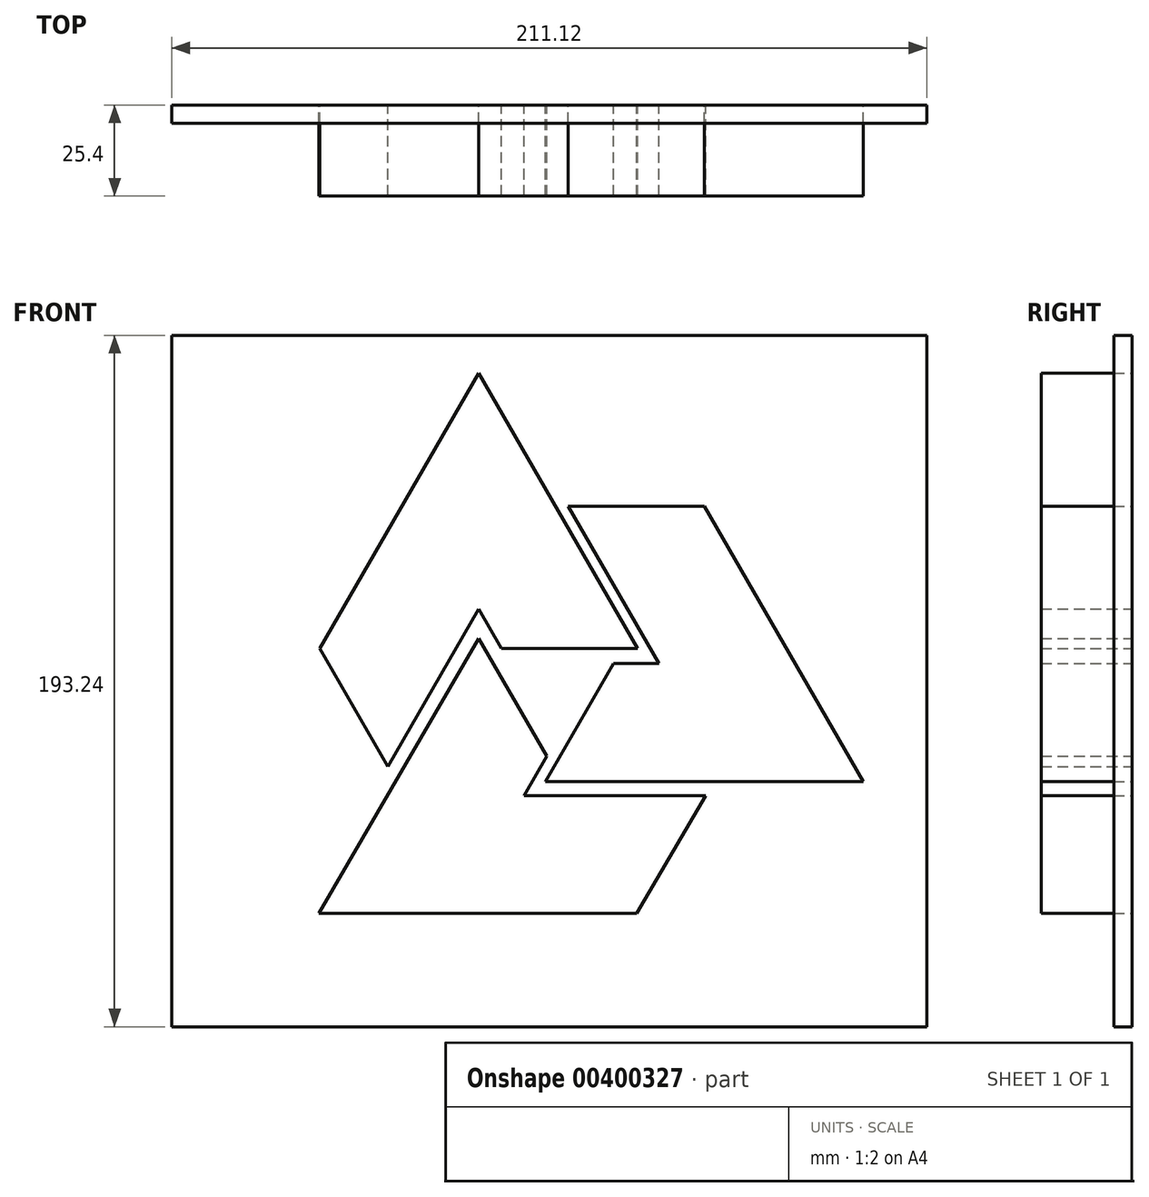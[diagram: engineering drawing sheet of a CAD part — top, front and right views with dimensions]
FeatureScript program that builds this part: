
annotation { "Feature Type Name" : "Feature", "Feature Type Description" : "" }
export const myFeature = defineFeature(function(context is Context, id is Id, definition is map)
    precondition{}
    {
        {
            var Q0;
            Q0=qCreatedBy(makeId("Front.planeOp"),FACE);
            var sketch = newSketch(context, id + "F0", { "sketchPlane" : qUnion([Q0])});
            skLineSegment(sketch, "E0", {"start": v(-33.33, -43.73) * mm, "end": v(55.57, -43.73) * mm});
            skLineSegment(sketch, "E1", {"start": v(55.57, -43.73) * mm, "end": v(74.77, -10.9) * mm});
            skLineSegment(sketch, "E2", {"start": v(-33.33, -43.73) * mm, "end": v(11.33, 33.14) * mm});
            skLineSegment(sketch, "E3", {"start": v(11.33, 33.14) * mm, "end": v(-26.15, -31.37) * mm});
            skLineSegment(sketch, "E4", {"start": v(74.77, -10.9) * mm, "end": v(23.97, -10.9) * mm});
            skLineSegment(sketch, "E5", {"start": v(23.97, -10.9) * mm, "end": v(30.38, 0.15) * mm});
            skLineSegment(sketch, "E6", {"start": v(30.38, 0.15) * mm, "end": v(11.33, 33.14) * mm});
            skLineSegment(sketch, "E7", {"start": v(11.33, 107.3) * mm, "end": v(-33.12, 30.32) * mm});
            skLineSegment(sketch, "E8", {"start": v(-33.12, 30.32) * mm, "end": v(-14.07, -2.68) * mm});
            skLineSegment(sketch, "E9", {"start": v(11.33, 107.3) * mm, "end": v(55.78, 30.32) * mm});
            skLineSegment(sketch, "E10", {"start": v(55.78, 30.32) * mm, "end": v(18.47, 94.93) * mm});
            skLineSegment(sketch, "E11", {"start": v(-14.07, -2.68) * mm, "end": v(11.33, 41.31) * mm});
            skLineSegment(sketch, "E12", {"start": v(11.33, 41.31) * mm, "end": v(17.68, 30.32) * mm});
            skLineSegment(sketch, "E13", {"start": v(17.68, 30.32) * mm, "end": v(55.78, 30.32) * mm});
            skLineSegment(sketch, "E14", {"start": v(118.9, -6.93) * mm, "end": v(74.44, 70.06) * mm});
            skLineSegment(sketch, "E15", {"start": v(74.44, 70.06) * mm, "end": v(36.34, 70.06) * mm});
            skLineSegment(sketch, "E16", {"start": v(118.9, -6.93) * mm, "end": v(30, -6.93) * mm});
            skLineSegment(sketch, "E17", {"start": v(30, -6.93) * mm, "end": v(104.6, -6.93) * mm});
            skLineSegment(sketch, "E18", {"start": v(36.34, 70.06) * mm, "end": v(61.74, 26.06) * mm});
            skLineSegment(sketch, "E19", {"start": v(61.74, 26.06) * mm, "end": v(49.04, 26.06) * mm});
            skLineSegment(sketch, "E20", {"start": v(49.04, 26.06) * mm, "end": v(30, -6.93) * mm});
            skSolve(sketch);
        }
        {
            var Q0;
            Q0=qCreatedBy(makeId("Front.planeOp"),FACE);
            var sketch = newSketch(context, id + "F1", { "sketchPlane" : qUnion([Q0])});
            skLineSegment(sketch, "E21.bottom", {"start": v(-74.5, 117.8) * mm, "end": v(136.63, 117.8) * mm});
            skLineSegment(sketch, "E21.top", {"start": v(-74.5, -75.45) * mm, "end": v(136.63, -75.45) * mm});
            skLineSegment(sketch, "E21.left", {"start": v(-74.5, 117.8) * mm, "end": v(-74.5, -75.45) * mm});
            skLineSegment(sketch, "E21.right", {"start": v(136.63, 117.8) * mm, "end": v(136.63, -75.45) * mm});
            skSolve(sketch);
        }
        {
            var Q0;
            Q0=makeQuery(id+"F1.imprint","IMPRINT",FACE,{"disambiguationData":[TD([[makeQuery(id+"F1.imprint","IMPRINT",EDGE,{"derivedFrom":sQuery(id+"F1.wireOp",EDGE,"E21.bottom")}),-1.0]])]});
            extrude(context, id + "F2", {"entities" : qUnion([Q0]), "depth" : 5.08 * mm});
        }
        {
            var Q0;
            Q0 = qSketchRegion(id + "F0", true);
            extrude(context, id + "F3", {"entities" : qUnion([Q0]), "depth" : 25.4 * mm});
        }
    });
